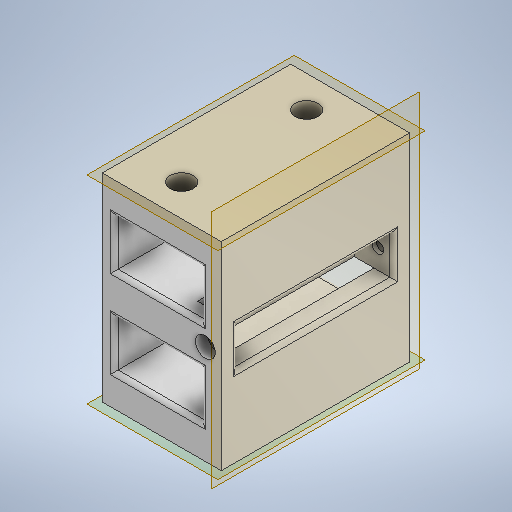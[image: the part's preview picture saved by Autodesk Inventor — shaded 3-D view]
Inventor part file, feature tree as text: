
AUTODESK INVENTOR PART (.ipt)
format: ipt  version: 2025.2 (Build 292293000, 293)  size: 535,040 bytes
history: native  units: mm
features: sketch x8, extrude x5, other x4, hole x3, fillet x2
ambient origin geometry x8: Origin, YZ Plane, XZ Plane, XY Plane, X Axis, Y Axis, Z Axis, Center Point
bodies: Body1 (feature_tree)
feature tree (22):
  other  "ソリッド1"
  extrude  "押し出し1"  Depth=30.0mm
  other  "作業平面1"
  extrude  "押し出し2"  Depth=47.5mm
  extrude  "押し出し3"  Depth=50.0mm TaperAngle=0.0deg
  other  "作業平面2"
  hole  "穴1"  [1 undecoded]
  hole  "穴2"  [1 undecoded]
  extrude  "押し出し4"  Depth=10.0mm
  extrude  "押し出し5"  TaperAngle=0.0deg  [1 undecoded]
  fillet  "フィレット1"  [1 undecoded]
  fillet  "フィレット2"  Radius=10.0mm
  other  "作業平面3"
  hole  "穴3"  [1 undecoded]
  sketch  "スケッチ1"
  sketch  "スケッチ2"
  sketch  "スケッチ3"
  sketch  "スケッチ4"
  sketch  "スケッチ5"
  sketch  "スケッチ6"
  sketch  "スケッチ7"
  sketch  "スケッチ8"
note: 5 required parameter values undecoded (feature->parameter linkage not recoverable at this tier; creation-order binding heuristic only, values carry confidence <= 0.55)
